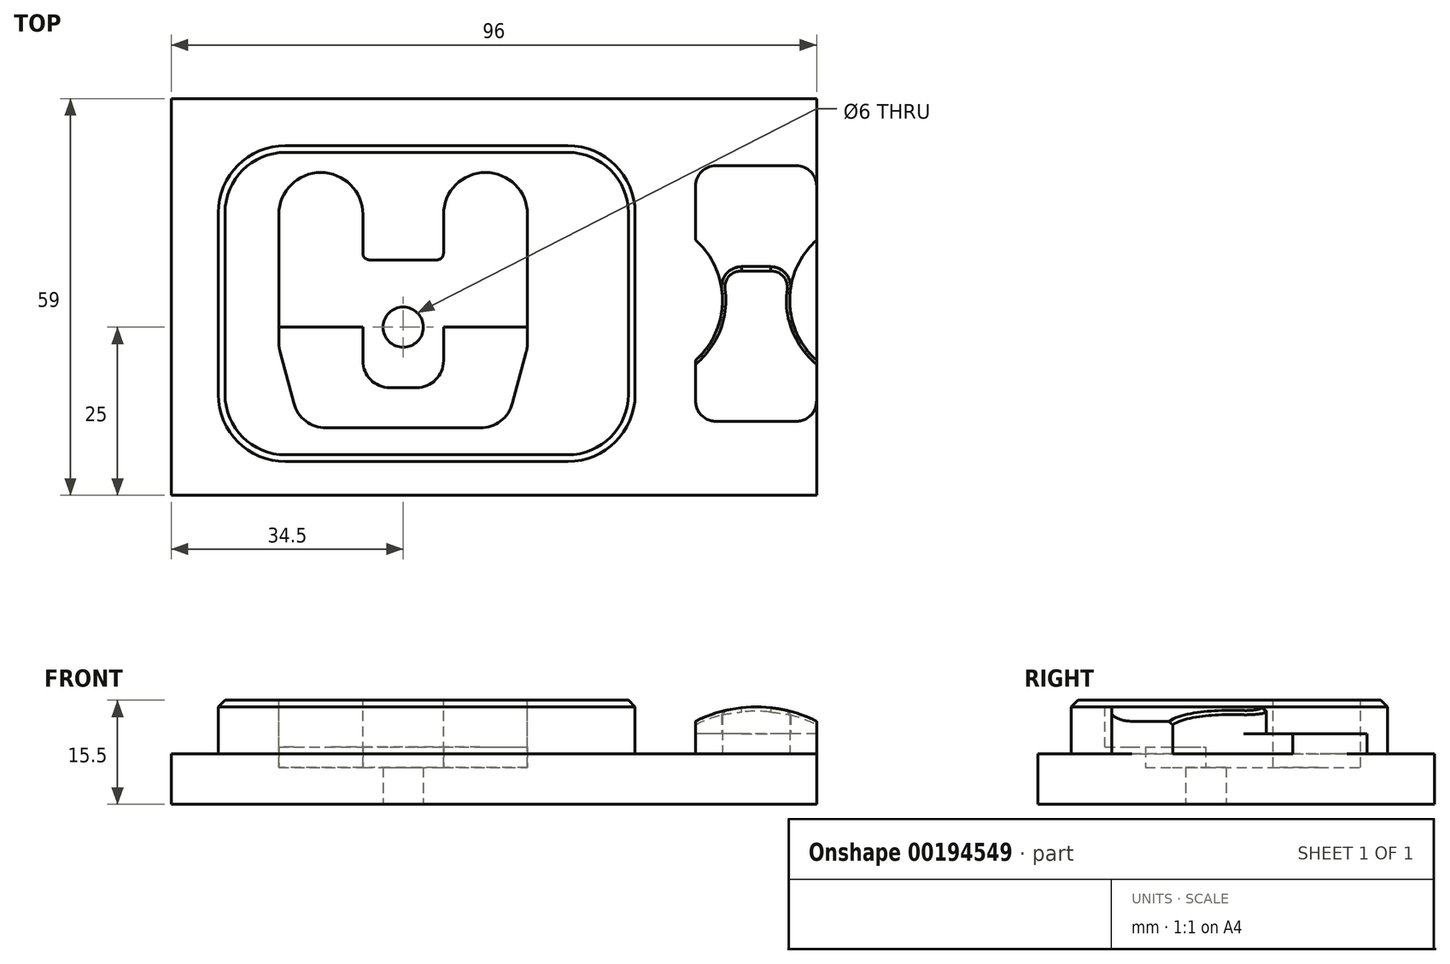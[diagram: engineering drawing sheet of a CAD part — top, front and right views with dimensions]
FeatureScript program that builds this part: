
annotation { "Feature Type Name" : "Feature", "Feature Type Description" : "" }
export const myFeature = defineFeature(function(context is Context, id is Id, definition is map)
    precondition{}
    {
        {
            var Q0;
            Q0=qCreatedBy(makeId("Top.planeOp"),FACE);
            var sketch = newSketch(context, id + "F0", { "sketchPlane" : qUnion([Q0])});
            skLineSegment(sketch, "E0.bottom", {"start": v(0, 0) * mm, "end": v(96, 0) * mm});
            skLineSegment(sketch, "E0.top", {"start": v(0, 59) * mm, "end": v(96, 59) * mm});
            skLineSegment(sketch, "E0.left", {"start": v(0, 0) * mm, "end": v(0, 59) * mm});
            skLineSegment(sketch, "E0.right", {"start": v(96, 0) * mm, "end": v(96, 59) * mm});
            skSolve(sketch);
        }
        {
            var Q0;
            Q0 = qSketchRegion(id + "F0", true);
            extrude(context, id + "F1", {"entities" : qUnion([Q0]), "oppositeDirection" : true, "depth" : 15.5 * mm, "offsetDistance" : 25 * mm});
        }
        {
            var Q0;
            Q0=makeQuery(id+"F1.opExtrude","CAP_FACE",FACE,{"disambiguationData":[OSD([sQuery(id+"F0.wireOp",EDGE,"E0.bottom"),sQuery(id+"F0.wireOp",EDGE,"E0.top"),sQuery(id+"F0.wireOp",EDGE,"E0.left"),sQuery(id+"F0.wireOp",EDGE,"E0.right")])],"isStart":true});
            var sketch = newSketch(context, id + "F2", { "sketchPlane" : qUnion([Q0])});
            skLineSegment(sketch, "E1.bottom", {"start": v(7, 5) * mm, "end": v(69, 5) * mm});
            skLineSegment(sketch, "E1.top", {"start": v(7, 52) * mm, "end": v(69, 52) * mm});
            skLineSegment(sketch, "E1.left", {"start": v(7, 5) * mm, "end": v(7, 52) * mm});
            skLineSegment(sketch, "E1.right", {"start": v(69, 5) * mm, "end": v(69, 52) * mm});
            skLineSegment(sketch, "E2", {"start": v(34.5, 10) * mm, "end": v(19.22, 10) * mm});
            skLineSegment(sketch, "E3", {"start": v(19.22, 10) * mm, "end": v(16, 22) * mm});
            skLineSegment(sketch, "E4", {"start": v(16, 22) * mm, "end": v(16, 41.75) * mm});
            skLineSegment(sketch, "E5", {"start": v(28.5, 41.75) * mm, "end": v(28.5, 35) * mm});
            skLineSegment(sketch, "E6", {"start": v(28.5, 35) * mm, "end": v(34.5, 35) * mm});
            skLineSegment(sketch, "E7", {"start": v(34.5, 8.84) * mm, "end": v(34.5, 44.06) * mm, "construction": true});
            skLineSegment(sketch, "E8.MirrorCS", {"start": v(40.5, 41.75) * mm, "end": v(40.5, 35) * mm});
            skLineSegment(sketch, "E9.MirrorCS", {"start": v(40.5, 35) * mm, "end": v(34.5, 35) * mm});
            skLineSegment(sketch, "E10.MirrorCS", {"start": v(49.78, 10) * mm, "end": v(53, 22) * mm});
            skLineSegment(sketch, "E11.MirrorCS", {"start": v(34.5, 10) * mm, "end": v(49.78, 10) * mm});
            skLineSegment(sketch, "E12.MirrorCS", {"start": v(53, 22) * mm, "end": v(53, 41.75) * mm});
            skArc(sketch, "E13", {"start": v(28.5, 41.75) * mm, "mid": v(22.25, 48) * mm, "end": v(16, 41.75) * mm});
            skArc(sketch, "E14.MirrorC", {"start": v(40.5, 41.75) * mm, "mid": v(46.75, 48) * mm, "end": v(53, 41.75) * mm});
            skSolve(sketch);
        }
        {
            var Q0;
            Q0=makeQuery(id+"F2.imprint","IMPRINT",FACE,{"disambiguationData":[TD([[makeQuery(id+"F2.imprint","IMPRINT",EDGE,{"derivedFrom":sQuery(id+"F2.wireOp",EDGE,"E1.bottom")}),-1.0]])]});
            extrude(context, id + "F3", {"entities" : qUnion([Q0]), "operationType" : NewBodyOperationType.REMOVE, "oppositeDirection" : true, "depth" : (15.5 - 7.5) * mm, "offsetDistance" : 25 * mm});
        }
        {
            var Q0;
            Q0=makeQuery(id+"F2.imprint","IMPRINT",FACE,{"disambiguationData":[TD([[makeQuery(id+"F2.imprint","IMPRINT",EDGE,{"derivedFrom":sQuery(id+"F2.wireOp",EDGE,"E2")}),-1.0]])]});
            extrude(context, id + "F4", {"entities" : qUnion([Q0]), "operationType" : NewBodyOperationType.REMOVE, "oppositeDirection" : true, "depth" : 10 * mm, "offsetDistance" : 25 * mm});
        }
        {
            var Q0;
            Q0=makeQuery(id+"F4.boolean.opBoolean","COPY",FACE,{"derivedFrom":makeQuery(id+"F4.opExtrude","CAP_FACE",FACE,{"disambiguationData":[OSD([sQuery(id+"F2.wireOp",EDGE,"E2"),sQuery(id+"F2.wireOp",EDGE,"E3"),sQuery(id+"F2.wireOp",EDGE,"E4"),sQuery(id+"F2.wireOp",EDGE,"E5"),sQuery(id+"F2.wireOp",EDGE,"E6"),sQuery(id+"F2.wireOp",EDGE,"E8.MirrorCS"),sQuery(id+"F2.wireOp",EDGE,"E9.MirrorCS"),sQuery(id+"F2.wireOp",EDGE,"E10.MirrorCS"),sQuery(id+"F2.wireOp",EDGE,"E11.MirrorCS"),sQuery(id+"F2.wireOp",EDGE,"E12.MirrorCS"),sQuery(id+"F2.wireOp",EDGE,"E13"),sQuery(id+"F2.wireOp",EDGE,"E14.MirrorC")])],"isStart":false})});
            var sketch = newSketch(context, id + "F5", { "sketchPlane" : qUnion([Q0])});
            skArc(sketch, "E15.0.0", {"start": v(53, 41.75) * mm, "mid": v(46.75, 48) * mm, "end": v(40.5, 41.75) * mm});
            skLineSegment(sketch, "E15.0.1", {"start": v(40.5, 41.75) * mm, "end": v(40.5, 35) * mm});
            skLineSegment(sketch, "E15.0.2", {"start": v(40.5, 35) * mm, "end": v(28.5, 35) * mm});
            skLineSegment(sketch, "E15.0.3", {"start": v(28.5, 35) * mm, "end": v(28.5, 41.75) * mm});
            skArc(sketch, "E15.0.4", {"start": v(28.5, 41.75) * mm, "mid": v(22.25, 48) * mm, "end": v(16, 41.75) * mm});
            skLineSegment(sketch, "E15.0.5", {"start": v(16, 41.75) * mm, "end": v(16, 22) * mm});
            skLineSegment(sketch, "E15.0.6", {"start": v(16, 22) * mm, "end": v(19.22, 10) * mm});
            skLineSegment(sketch, "E15.0.7", {"start": v(19.22, 10) * mm, "end": v(49.78, 10) * mm});
            skLineSegment(sketch, "E15.0.8", {"start": v(49.78, 10) * mm, "end": v(53, 22) * mm});
            skLineSegment(sketch, "E15.0.9", {"start": v(53, 22) * mm, "end": v(53, 41.75) * mm});
            skLineSegment(sketch, "E16", {"start": v(16, 25) * mm, "end": v(28.5, 25) * mm});
            skLineSegment(sketch, "E17", {"start": v(28.5, 25) * mm, "end": v(28.5, 16) * mm});
            skLineSegment(sketch, "E18", {"start": v(28.5, 16) * mm, "end": v(40.5, 16) * mm});
            skLineSegment(sketch, "E19", {"start": v(40.5, 16) * mm, "end": v(40.5, 25) * mm});
            skLineSegment(sketch, "E20", {"start": v(40.5, 25) * mm, "end": v(53, 25) * mm});
            skLineSegment(sketch, "E21", {"start": v(28.5, 25) * mm, "end": v(40.5, 25) * mm, "construction": true});
            skPoint(sketch, "E22", {"position": v(34.5, 25) * mm});
            skSolve(sketch);
        }
        {
            var Q0;
            {var subQ1=sQuery(id+"F5.wireOp",EDGE,"E15.0.6");Q0=makeQuery(id+"F5.imprint","IMPRINT",FACE,{"disambiguationData":[TD([[makeQuery(id+"F5.imprint","IMPRINT",EDGE,{"derivedFrom":subQ1}),-1.0]])]});}
            extrude(context, id + "F6", {"entities" : qUnion([Q0]), "operationType" : NewBodyOperationType.ADD, "depth" : (10 - 7) * mm, "offsetDistance" : 25 * mm});
        }
        {
            var Q0;
            Q0=makeQuery(id+"F3.boolean.opBoolean","COPY",EDGE,{"derivedFrom":makeQuery(id+"F3.opExtrude","SWEPT_EDGE",EDGE,{"disambiguationData":[OSD([sQuery(id+"F2.wireOp",EDGE,"E1.bottom"),sQuery(id+"F2.wireOp",EDGE,"E1.left")])]})});
            var Q1;
            Q1=makeQuery(id+"F3.boolean.opBoolean","COPY",EDGE,{"derivedFrom":makeQuery(id+"F3.opExtrude","SWEPT_EDGE",EDGE,{"disambiguationData":[OSD([sQuery(id+"F2.wireOp",EDGE,"E1.bottom"),sQuery(id+"F2.wireOp",EDGE,"E1.right")])]})});
            var Q2;
            Q2=makeQuery(id+"F3.boolean.opBoolean","COPY",EDGE,{"derivedFrom":makeQuery(id+"F3.opExtrude","SWEPT_EDGE",EDGE,{"disambiguationData":[OSD([sQuery(id+"F2.wireOp",EDGE,"E1.top"),sQuery(id+"F2.wireOp",EDGE,"E1.right")])]})});
            var Q3;
            Q3=makeQuery(id+"F3.boolean.opBoolean","COPY",EDGE,{"derivedFrom":makeQuery(id+"F3.opExtrude","SWEPT_EDGE",EDGE,{"disambiguationData":[OSD([sQuery(id+"F2.wireOp",EDGE,"E1.top"),sQuery(id+"F2.wireOp",EDGE,"E1.left")])]})});
            fillet(context, id + "F7", {"entities" : qUnion([Q0, Q1, Q2, Q3]), "tangentPropagation" : true, "radius" : 10 * mm, "defaultsChanged" : false, "vertexSettings" : [], "allowEdgeOverflow" : false});
        }
        {
            var Q0;
            Q0=makeQuery(id+"F6.opExtrude","SWEPT_EDGE",EDGE,{"disambiguationData":[OSD([sQuery(id+"F5.wireOp",EDGE,"E15.0.5"),sQuery(id+"F5.wireOp",EDGE,"E16")])]});
            var Q1;
            Q1=makeQuery(id+"F6.opExtrude","SWEPT_EDGE",EDGE,{"disambiguationData":[OSD([sQuery(id+"F5.wireOp",EDGE,"E15.0.9"),sQuery(id+"F5.wireOp",EDGE,"E20")])]});
            var Q2;
            Q2=makeQuery(id+"F6.opExtrude","SWEPT_EDGE",EDGE,{"disambiguationData":[OSD([sQuery(id+"F5.wireOp",EDGE,"E17"),sQuery(id+"F5.wireOp",EDGE,"E18")])]});
            var Q3;
            Q3=makeQuery(id+"F6.opExtrude","SWEPT_EDGE",EDGE,{"disambiguationData":[OSD([sQuery(id+"F5.wireOp",EDGE,"E18"),sQuery(id+"F5.wireOp",EDGE,"E19")])]});
            fillet(context, id + "F8", {"entities" : qUnion([Q0, Q1, Q2, Q3]), "tangentPropagation" : true, "radius" : 4 * mm, "defaultsChanged" : false, "vertexSettings" : [], "allowEdgeOverflow" : false});
        }
        {
            var Q0;
            Q0=makeQuery(id+"F4.boolean.opBoolean","COPY",EDGE,{"derivedFrom":makeQuery(id+"F4.opExtrude","SWEPT_EDGE",EDGE,{"disambiguationData":[OSD([sQuery(id+"F2.wireOp",EDGE,"E3"),sQuery(id+"F2.wireOp",EDGE,"E4")])]})});
            var Q1;
            Q1=makeQuery(id+"F4.boolean.opBoolean","COPY",EDGE,{"derivedFrom":makeQuery(id+"F4.opExtrude","SWEPT_EDGE",EDGE,{"disambiguationData":[OSD([sQuery(id+"F2.wireOp",EDGE,"E10.MirrorCS"),sQuery(id+"F2.wireOp",EDGE,"E12.MirrorCS")])]})});
            fillet(context, id + "F9", {"entities" : qUnion([Q0, Q1]), "tangentPropagation" : true, "radius" : 6 * mm, "defaultsChanged" : false, "vertexSettings" : [], "allowEdgeOverflow" : false});
        }
        {
            var Q0;
            Q0=makeQuery(id+"F4.boolean.opBoolean","COPY",EDGE,{"derivedFrom":makeQuery(id+"F4.opExtrude","SWEPT_EDGE",EDGE,{"disambiguationData":[OSD([sQuery(id+"F2.wireOp",EDGE,"E2"),sQuery(id+"F2.wireOp",EDGE,"E3")])]})});
            var Q1;
            Q1=makeQuery(id+"F4.boolean.opBoolean","COPY",EDGE,{"derivedFrom":makeQuery(id+"F4.opExtrude","SWEPT_EDGE",EDGE,{"disambiguationData":[OSD([sQuery(id+"F2.wireOp",EDGE,"E10.MirrorCS"),sQuery(id+"F2.wireOp",EDGE,"E11.MirrorCS")])]})});
            fillet(context, id + "F10", {"entities" : qUnion([Q0, Q1]), "tangentPropagation" : true, "radius" : 5 * mm, "defaultsChanged" : false, "vertexSettings" : [], "allowEdgeOverflow" : false});
        }
        {
            var Q0;
            Q0=makeQuery(id+"F4.boolean.opBoolean","COPY",EDGE,{"derivedFrom":makeQuery(id+"F4.opExtrude","SWEPT_EDGE",EDGE,{"disambiguationData":[OSD([sQuery(id+"F2.wireOp",EDGE,"E5"),sQuery(id+"F2.wireOp",EDGE,"E6")])]})});
            var Q1;
            Q1=makeQuery(id+"F4.boolean.opBoolean","COPY",EDGE,{"derivedFrom":makeQuery(id+"F4.opExtrude","SWEPT_EDGE",EDGE,{"disambiguationData":[OSD([sQuery(id+"F2.wireOp",EDGE,"E8.MirrorCS"),sQuery(id+"F2.wireOp",EDGE,"E9.MirrorCS")])]})});
            fillet(context, id + "F11", {"entities" : qUnion([Q0, Q1]), "tangentPropagation" : true, "radius" : 1 * mm, "defaultsChanged" : false, "vertexSettings" : [], "allowEdgeOverflow" : false});
        }
        {
            var Q0;
            Q0=sQuery(id+"F5.wireOp",VERTEX,"E22");
            var Q1;
            Q1=makeQuery(id+"F1.opExtrude","SWEPT_BODY",BODY,{"disambiguationData":[OSD([sQuery(id+"F0.wireOp",EDGE,"E0.bottom"),sQuery(id+"F0.wireOp",EDGE,"E0.top"),sQuery(id+"F0.wireOp",EDGE,"E0.left"),sQuery(id+"F0.wireOp",EDGE,"E0.right")])]});
            hole(context, id + "F12", {"style" : HoleStyle.SIMPLE, "endStyle" : HoleEndStyle.THROUGH, "holeDiameter" : 6 * mm, "majorDiameter" : 5 * mm, "tappedDepth" : 12 * mm, "tapClearance" : 3, "locations" : qUnion([Q0]), "scope" : qUnion([Q1]), "startStyle" : HoleStartStyle.SKETCH});
        }
        {
            var Q0;
            Q0=makeQuery(id+"F7.opFillet","BLEND_EDGE",EDGE,{"blendedFrom":[makeQuery(id+"F3.boolean.opBoolean","COPY",EDGE,{"derivedFrom":makeQuery(id+"F3.opExtrude","SWEPT_EDGE",EDGE,{"disambiguationData":[OSD([sQuery(id+"F2.wireOp",EDGE,"E1.bottom"),sQuery(id+"F2.wireOp",EDGE,"E1.right")])]})}),makeQuery(id+"F1.opExtrude","CAP_FACE",FACE,{"disambiguationData":[OSD([sQuery(id+"F0.wireOp",EDGE,"E0.bottom"),sQuery(id+"F0.wireOp",EDGE,"E0.top"),sQuery(id+"F0.wireOp",EDGE,"E0.left"),sQuery(id+"F0.wireOp",EDGE,"E0.right")])],"isStart":true})],"blendedInto":[makeQuery(id+"F1.opExtrude","CAP_FACE",FACE,{"disambiguationData":[OSD([sQuery(id+"F0.wireOp",EDGE,"E0.bottom"),sQuery(id+"F0.wireOp",EDGE,"E0.top"),sQuery(id+"F0.wireOp",EDGE,"E0.left"),sQuery(id+"F0.wireOp",EDGE,"E0.right")])],"isStart":true})]});
            chamfer(context, id + "F13", {"entities" : qUnion([Q0]), "width" : 1 * mm, "tangentPropagation" : true});
        }
        {
            var Q0;
            Q0=makeQuery(id+"F3.boolean.opBoolean","COPY",FACE,{"derivedFrom":makeQuery(id+"F3.opExtrude","CAP_FACE",FACE,{"disambiguationData":[OSD([sQuery(id+"F0.wireOp",EDGE,"E0.bottom"),sQuery(id+"F0.wireOp",EDGE,"E0.top"),sQuery(id+"F0.wireOp",EDGE,"E0.left"),sQuery(id+"F0.wireOp",EDGE,"E0.right"),sQuery(id+"F2.wireOp",EDGE,"E1.bottom"),sQuery(id+"F2.wireOp",EDGE,"E1.top"),sQuery(id+"F2.wireOp",EDGE,"E1.left"),sQuery(id+"F2.wireOp",EDGE,"E1.right")])],"isStart":false})});
            var sketch = newSketch(context, id + "F14", { "sketchPlane" : qUnion([Q0])});
            skLineSegment(sketch, "E23", {"start": v(87, 52.45) * mm, "end": v(87, 7.55) * mm, "construction": true});
            skLineSegment(sketch, "E24", {"start": v(104, 51.14) * mm, "end": v(104, 7.26) * mm, "construction": true});
            skLineSegment(sketch, "E25.bottom", {"start": v(96, 49) * mm, "end": v(78, 49) * mm});
            skLineSegment(sketch, "E25.top", {"start": v(96, 11) * mm, "end": v(78, 11) * mm});
            skLineSegment(sketch, "E25.left", {"start": v(96, 49) * mm, "end": v(96, 37.94) * mm});
            skLineSegment(sketch, "E25.right", {"start": v(78, 49) * mm, "end": v(78, 37.94) * mm});
            skPoint(sketch, "E25.middle", {"position": v(87, 30) * mm});
            skArc(sketch, "E26", {"start": v(96, 37.94) * mm, "mid": v(92, 29) * mm, "end": v(96, 20.06) * mm});
            skArc(sketch, "E27.MirrorCS", {"start": v(78, 37.94) * mm, "mid": v(82, 29) * mm, "end": v(78, 20.06) * mm});
            skLineSegment(sketch, "E28.trimOffspring", {"start": v(96, 20.06) * mm, "end": v(96, 11) * mm});
            skLineSegment(sketch, "E29.trimOffspring", {"start": v(78, 20.06) * mm, "end": v(78, 11) * mm});
            skLineSegment(sketch, "E30", {"start": v(80.9, 34) * mm, "end": v(93.1, 34) * mm});
            skSolve(sketch);
        }
        {
            var Q0;
            Q0=makeQuery(id+"F14.imprint","IMPRINT",FACE,{"disambiguationData":[TD([[makeQuery(id+"F14.imprint","IMPRINT",EDGE,{"derivedFrom":sQuery(id+"F14.wireOp",EDGE,"E25.bottom")}),1.0]])]});
            extrude(context, id + "F15", {"entities" : qUnion([Q0]), "operationType" : NewBodyOperationType.ADD, "depth" : 3 * mm, "offsetDistance" : 25 * mm});
        }
        {
            var Q0;
            Q0=makeQuery(id+"F14.imprint","IMPRINT",FACE,{"disambiguationData":[TD([[makeQuery(id+"F14.imprint","IMPRINT",EDGE,{"derivedFrom":sQuery(id+"F14.wireOp",EDGE,"E25.top")}),-1.0]])]});
            extrude(context, id + "F16", {"entities" : qUnion([Q0]), "operationType" : NewBodyOperationType.ADD, "depth" : (14.5 - 7.5) * mm, "offsetDistance" : 25 * mm});
        }
        {
            var Q0;
            Q0=makeQuery(id+"F15.opExtrude","SWEPT_EDGE",EDGE,{"disambiguationData":[OSD([sQuery(id+"F14.wireOp",EDGE,"E25.bottom"),sQuery(id+"F14.wireOp",EDGE,"E25.left")])]});
            var Q1;
            Q1=makeQuery(id+"F16.opExtrude","SWEPT_EDGE",EDGE,{"disambiguationData":[OSD([sQuery(id+"F14.wireOp",EDGE,"E26"),sQuery(id+"F14.wireOp",EDGE,"E30")])]});
            var Q2;
            Q2=makeQuery(id+"F16.opExtrude","SWEPT_EDGE",EDGE,{"disambiguationData":[OSD([sQuery(id+"F14.wireOp",EDGE,"E25.top"),sQuery(id+"F14.wireOp",EDGE,"E28.trimOffspring")])]});
            var Q3;
            Q3=makeQuery(id+"F16.opExtrude","SWEPT_EDGE",EDGE,{"disambiguationData":[OSD([sQuery(id+"F14.wireOp",EDGE,"E25.top"),sQuery(id+"F14.wireOp",EDGE,"E29.trimOffspring")])]});
            var Q4;
            Q4=makeQuery(id+"F16.opExtrude","SWEPT_EDGE",EDGE,{"disambiguationData":[OSD([sQuery(id+"F14.wireOp",EDGE,"E27.MirrorCS"),sQuery(id+"F14.wireOp",EDGE,"E30")])]});
            var Q5;
            Q5=makeQuery(id+"F15.opExtrude","SWEPT_EDGE",EDGE,{"disambiguationData":[OSD([sQuery(id+"F14.wireOp",EDGE,"E25.bottom"),sQuery(id+"F14.wireOp",EDGE,"E25.right")])]});
            fillet(context, id + "F17", {"entities" : qUnion([Q0, Q1, Q2, Q3, Q4, Q5]), "tangentPropagation" : true, "radius" : 3 * mm, "defaultsChanged" : false, "vertexSettings" : [], "allowEdgeOverflow" : false});
        }
        {
            var Q0;
            Q0=makeQuery(id+"F16.opExtrude","SWEPT_FACE",FACE,{"disambiguationData":[OSD([sQuery(id+"F14.wireOp",EDGE,"E25.top")])]});
            var sketch = newSketch(context, id + "F18", { "sketchPlane" : qUnion([Q0])});
            skArc(sketch, "E31", {"start": v(77.04, -3.66) * mm, "mid": v(87, -1) * mm, "end": v(96.96, -3.66) * mm});
            skPoint(sketch, "E31.centerSnap0", {"position": v(87, -8) * mm});
            skLineSegment(sketch, "E32", {"start": v(77.04, -3.66) * mm, "end": v(77.04, 3.73) * mm});
            skLineSegment(sketch, "E33", {"start": v(77.04, 3.73) * mm, "end": v(96.96, 3.73) * mm});
            skLineSegment(sketch, "E34", {"start": v(96.96, 3.73) * mm, "end": v(96.96, -3.66) * mm});
            skPoint(sketch, "E35", {"position": v(87, -1) * mm});
            skSolve(sketch);
        }
        {
            var Q0;
            Q0 = qSketchRegion(id + "F18", true);
            extrude(context, id + "F19", {"entities" : qUnion([Q0]), "operationType" : NewBodyOperationType.REMOVE, "endBound" : BoundingType.THROUGH_ALL, "oppositeDirection" : true, "depth" : 25 * mm, "offsetDistance" : 25 * mm});
        }
        {
            var Q0;
            Q0=makeQuery(id+"F19.boolean.opBoolean","COPY",EDGE,{"derivedFrom":makeQuery(id+"F19.opExtrude","CAP_EDGE",EDGE,{"disambiguationData":[OSD([sQuery(id+"F18.wireOp",EDGE,"E31")])],"isStart":true})});
            var Q1;
            {var subQ0=sQuery(id+"F14.wireOp",EDGE,"E26");Q1=makeQuery(id+"F19.boolean.opBoolean","INTERSECT",EDGE,{"derivedFrom":[makeQuery(id+"F16.boolean.opBoolean","MERGE",FACE,{"derivedFrom":[makeQuery(id+"F15.opExtrude","SWEPT_FACE",FACE,{"disambiguationData":[OSD([subQ0])]}),makeQuery(id+"F16.opExtrude","SWEPT_FACE",FACE,{"disambiguationData":[OSD([subQ0])]})]}),makeQuery(id+"F19.opExtrude","SWEPT_FACE",FACE,{"disambiguationData":[OSD([sQuery(id+"F18.wireOp",EDGE,"E31")])]})]});}
            chamfer(context, id + "F20", {"entities" : qUnion([Q0, Q1]), "width" : 0.5 * mm, "tangentPropagation" : true});
        }
    });
